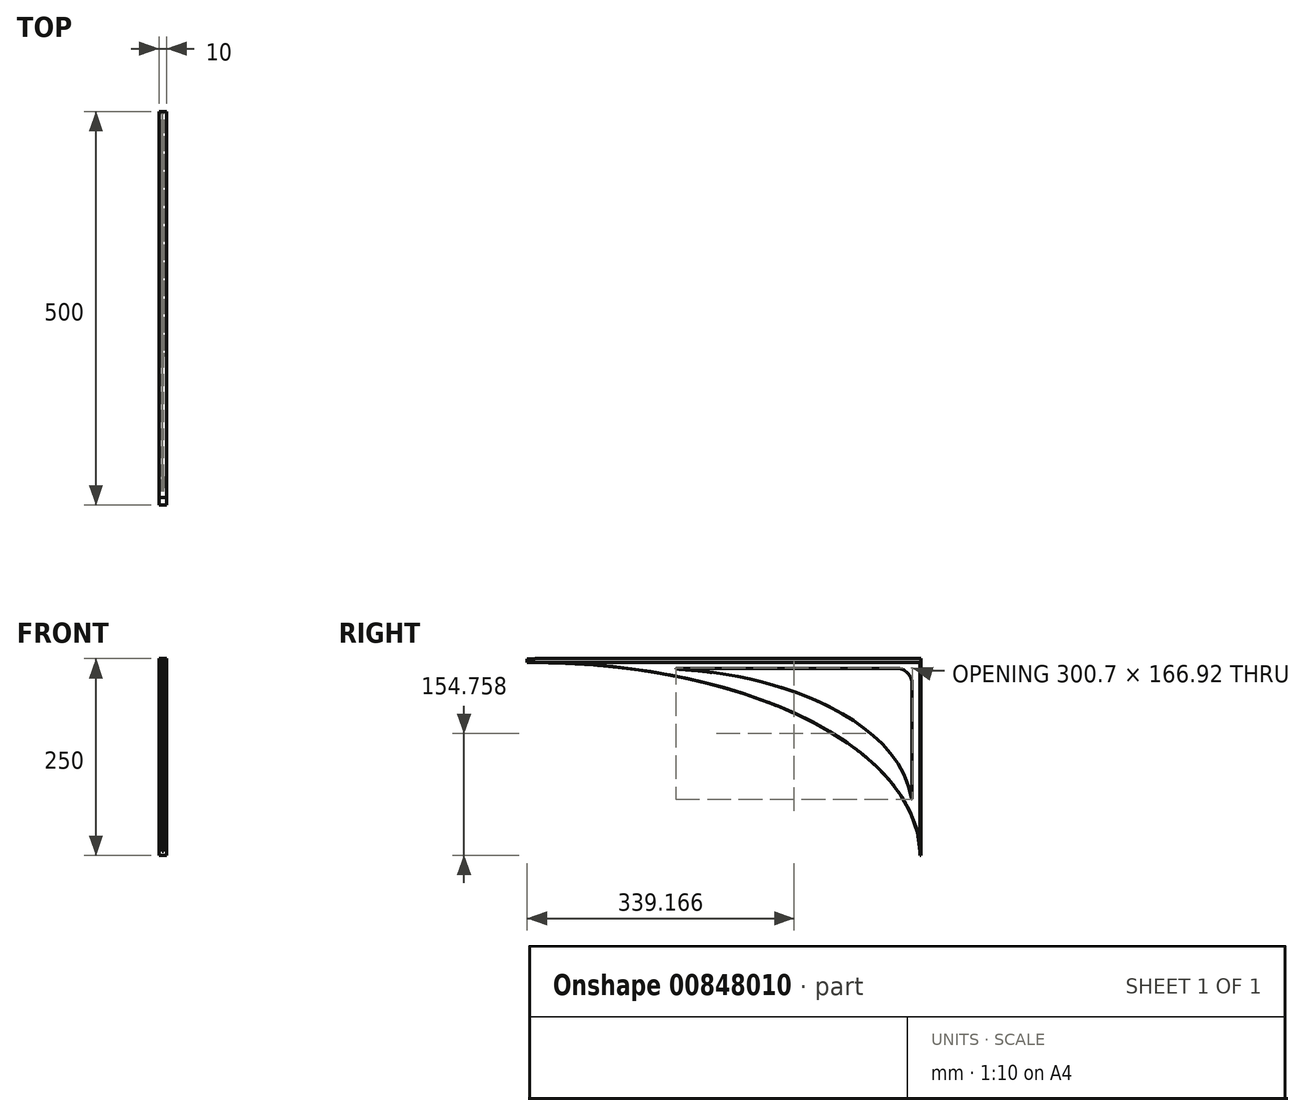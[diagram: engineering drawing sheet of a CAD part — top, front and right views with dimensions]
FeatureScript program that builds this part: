
annotation { "Feature Type Name" : "Feature", "Feature Type Description" : "" }
export const myFeature = defineFeature(function(context is Context, id is Id, definition is map)
    precondition{}
    {
        {
            var Q0;
            Q0=qCreatedBy(makeId("Front.planeOp"),FACE);
            var sketch = newSketch(context, id + "F0", { "sketchPlane" : qUnion([Q0])});
            skLineSegment(sketch, "E0.bottom", {"start": v(-5, -125) * mm, "end": v(5, -125) * mm});
            skLineSegment(sketch, "E0.top", {"start": v(-5, 125) * mm, "end": v(5, 125) * mm});
            skLineSegment(sketch, "E0.left", {"start": v(-5, -125) * mm, "end": v(-5, 125) * mm});
            skLineSegment(sketch, "E0.right", {"start": v(5, -125) * mm, "end": v(5, 125) * mm});
            skPoint(sketch, "E0.middle", {"position": v(0, 0) * mm});
            skLineSegment(sketch, "E1", {"start": v(-5, 120) * mm, "end": v(-5, 125) * mm});
            skLineSegment(sketch, "E2.MirrorCS", {"start": v(5, 120) * mm, "end": v(5, 125) * mm});
            skLineSegment(sketch, "E3", {"start": v(-5, 120) * mm, "end": v(5, 120) * mm});
            skSolve(sketch);
        }
        {
            var Q0;
            {var subQ0=sQuery(id+"F0.wireOp",EDGE,"E0.bottom");Q0=makeQuery(id+"F0.imprint","IMPRINT",FACE,{"disambiguationData":[TD([[makeQuery(id+"F0.imprint","IMPRINT",EDGE,{"derivedFrom":subQ0}),1.0]])]});}
            extrude(context, id + "F1", {"entities" : qUnion([Q0]), "depth" : 1 * mm, "offsetDistance" : 25 * mm});
        }
        {
            var Q0;
            {var subQ0=sQuery(id+"F0.wireOp",EDGE,"E0.top");Q0=makeQuery(id+"F0.imprint","IMPRINT",FACE,{"disambiguationData":[TD([[makeQuery(id+"F0.imprint","IMPRINT",EDGE,{"derivedFrom":subQ0}),-1.0]])]});}
            extrude(context, id + "F2", {"entities" : qUnion([Q0]), "operationType" : NewBodyOperationType.ADD, "depth" : 500 * mm, "offsetDistance" : 25 * mm});
        }
        {
            var Q0;
            Q0=makeQuery(id+"F2.opExtrude","SWEPT_FACE",FACE,{"disambiguationData":[OSD([sQuery(id+"F0.wireOp",EDGE,"E0.top")])]});
            var sketch = newSketch(context, id + "F3", { "sketchPlane" : qUnion([Q0])});
            skLineSegment(sketch, "E4.bottom", {"start": v(-5, -490) * mm, "end": v(5, -490) * mm});
            skLineSegment(sketch, "E4.top", {"start": v(-5, -500) * mm, "end": v(5, -500) * mm});
            skLineSegment(sketch, "E4.left", {"start": v(-5, -490) * mm, "end": v(-5, -500) * mm});
            skLineSegment(sketch, "E4.right", {"start": v(5, -490) * mm, "end": v(5, -500) * mm});
            skSolve(sketch);
        }
        {
            var Q0;
            Q0=makeQuery(id+"F3.imprint","IMPRINT",FACE,{"disambiguationData":[TD([[makeQuery(id+"F3.imprint","IMPRINT",EDGE,{"derivedFrom":sQuery(id+"F3.wireOp",EDGE,"E4.bottom")}),-1.0]])]});
            extrude(context, id + "F4", {"entities" : qUnion([Q0]), "operationType" : NewBodyOperationType.REMOVE, "oppositeDirection" : true, "depth" : 0.1 * mm, "offsetDistance" : 25 * mm});
        }
        {
            var Q0;
            Q0=qCreatedBy(makeId("Right.planeOp"),FACE);
            var sketch = newSketch(context, id + "F5", { "sketchPlane" : qUnion([Q0])});
            skLineSegment(sketch, "E5.bottom", {"start": v(-0.9, 120.07) * mm, "end": v(-493.8, 120.07) * mm});
            skLineSegment(sketch, "E5.left", {"start": v(-0.9, 120.07) * mm, "end": v(-0.9, -124.82) * mm});
            skLineSegment(sketch, "E6.left", {"start": v(-493.8, 120.07) * mm, "end": v(-493.8, 120.07) * mm});
            skEllipticalArc(sketch, "E7", {});
            const initialGuessF5  = {"E7": [-0.4937974512577056, -0.12481619417667389, 1, 0, 0.49289696163032193, 0.24488162249326706, 0, 1.5707963267948966]};
            skSetInitialGuess(sketch, initialGuessF5);
            skSolve(sketch);
        }
        {
            var Q0;
            Q0=makeQuery(id+"F5.imprint","IMPRINT",FACE,{"disambiguationData":[TD([[makeQuery(id+"F5.imprint","IMPRINT",EDGE,{"derivedFrom":sQuery(id+"F5.wireOp",EDGE,"E5.bottom")}),1.0]])]});
            extrude(context, id + "F6", {"entities" : qUnion([Q0]), "operationType" : NewBodyOperationType.ADD, "endBound" : BoundingType.SYMMETRIC, "depth" : 2 * mm, "offsetDistance" : 25 * mm});
        }
        {
            var Q0;
            Q0=makeQuery(id+"F6.boolean.opBoolean","INTERSECT",EDGE,{"derivedFrom":[makeQuery(id+"F2.opExtrude","SWEPT_FACE",FACE,{"disambiguationData":[OSD([sQuery(id+"F0.wireOp",EDGE,"E3")])]}),makeQuery(id+"F6.opExtrude","CAP_FACE",FACE,{"disambiguationData":[OSD([sQuery(id+"F5.wireOp",EDGE,"E5.bottom"),sQuery(id+"F5.wireOp",EDGE,"E5.left"),sQuery(id+"F5.wireOp",EDGE,"E7")])],"isStart":false})]});
            var Q1;
            Q1=makeQuery(id+"F6.boolean.opBoolean","INTERSECT",EDGE,{"derivedFrom":[makeQuery(id+"F2.opExtrude","SWEPT_FACE",FACE,{"disambiguationData":[OSD([sQuery(id+"F0.wireOp",EDGE,"E3")])]}),makeQuery(id+"F6.opExtrude","CAP_FACE",FACE,{"disambiguationData":[OSD([sQuery(id+"F5.wireOp",EDGE,"E5.bottom"),sQuery(id+"F5.wireOp",EDGE,"E5.left"),sQuery(id+"F5.wireOp",EDGE,"E7")])],"isStart":true})]});
            fillet(context, id + "F7", {"entities" : qUnion([Q0, Q1]), "radius" : .2 * mm, "tangentPropagation" : true, "allowEdgeOverflow" : false});
        }
        {
            var Q0;
            Q0=makeQuery(id+"F6.boolean.opBoolean","INTERSECT",EDGE,{"derivedFrom":[makeQuery(id+"F2.opExtrude","SWEPT_FACE",FACE,{"disambiguationData":[OSD([sQuery(id+"F0.wireOp",EDGE,"E3")])]}),makeQuery(id+"F6.opExtrude","SWEPT_FACE",FACE,{"disambiguationData":[OSD([sQuery(id+"F5.wireOp",EDGE,"E7")])]})]});
            fillet(context, id + "F8", {"entities" : qUnion([Q0]), "radius" : 0.1 * mm, "tangentPropagation" : true, "allowEdgeOverflow" : false});
        }
        {
            var Q0;
            Q0=makeQuery(id+"F6.opExtrude","CAP_EDGE",EDGE,{"disambiguationData":[OSD([sQuery(id+"F5.wireOp",EDGE,"E7")])],"isStart":true});
            var Q1;
            Q1=makeQuery(id+"F6.boolean.opBoolean","SPLIT",EDGE,{"derivedFrom":makeQuery(id+"F6.opExtrude","CAP_EDGE",EDGE,{"disambiguationData":[OSD([sQuery(id+"F5.wireOp",EDGE,"E7")])],"isStart":false})});
            fillet(context, id + "F9", {"entities" : qUnion([Q0, Q1]), "radius" : 0.2 * mm, "tangentPropagation" : true, "allowEdgeOverflow" : false});
        }
        {
            var Q0;
            Q0=makeQuery(id+"F6.opExtrude","CAP_FACE",FACE,{"disambiguationData":[OSD([sQuery(id+"F5.wireOp",EDGE,"E5.bottom"),sQuery(id+"F5.wireOp",EDGE,"E5.left"),sQuery(id+"F5.wireOp",EDGE,"E7")])],"isStart":true});
            var sketch = newSketch(context, id + "F10", { "sketchPlane" : qUnion([Q0])});
            skLineSegment(sketch, "E8.bottom", {"start": v(30.98, 112.72) * mm, "end": v(345.48, 112.72) * mm});
            skLineSegment(sketch, "E8.left", {"start": v(10.98, 92.72) * mm, "end": v(10.98, -66.6) * mm});
            skEllipticalArc(sketch, "E9", {});
            skEllipticalArc(sketch, "E10", {});
            const initialGuessF10  = {"E9": [0.34547726979778404, -0.0665975014916268, 0, 1, 0.17931767315689862, 0.3344950337395309, 6.283185307179586, 1.5707963267948966], "E10": [0.03098223605825314, 0.09272017166527183, 0, 1, 0.02, 0.02, 6.283185307179586, 1.5707963267948966]};
            skSetInitialGuess(sketch, initialGuessF10);
            skSolve(sketch);
        }
        {
            var Q0;
            Q0=makeQuery(id+"F10.imprint","IMPRINT",FACE,{"disambiguationData":[TD([[makeQuery(id+"F10.imprint","IMPRINT",EDGE,{"derivedFrom":sQuery(id+"F10.wireOp",EDGE,"E8.bottom")}),-1.0]])]});
            extrude(context, id + "F11", {"entities" : qUnion([Q0]), "operationType" : NewBodyOperationType.REMOVE, "endBound" : BoundingType.SYMMETRIC, "oppositeDirection" : true, "depth" : 4 * mm, "offsetDistance" : 25 * mm});
        }
        {
            var Q0;
            Q0=makeQuery(id+"F11.boolean.opBoolean","COPY",EDGE,{"derivedFrom":makeQuery(id+"F11.opExtrude","SWEPT_EDGE",EDGE,{"disambiguationData":[OSD([sQuery(id+"F10.wireOp",EDGE,"E8.bottom"),sQuery(id+"F10.wireOp",EDGE,"E8.left")])]})});
            fillet(context, id + "F12", {"entities" : qUnion([Q0]), "radius" : 0.5 * mm, "tangentPropagation" : true, "allowEdgeOverflow" : false});
        }
        {
            var Q0;
            Q0=makeQuery(id+"F11.boolean.opBoolean","COPY",FACE,{"derivedFrom":makeQuery(id+"F11.opExtrude","SWEPT_FACE",FACE,{"disambiguationData":[OSD([sQuery(id+"F10.wireOp",EDGE,"E9")])]})});
            fillet(context, id + "F13", {"entities" : qUnion([Q0]), "radius" : 0.5 * mm, "tangentPropagation" : true, "allowEdgeOverflow" : false});
        }
    });
